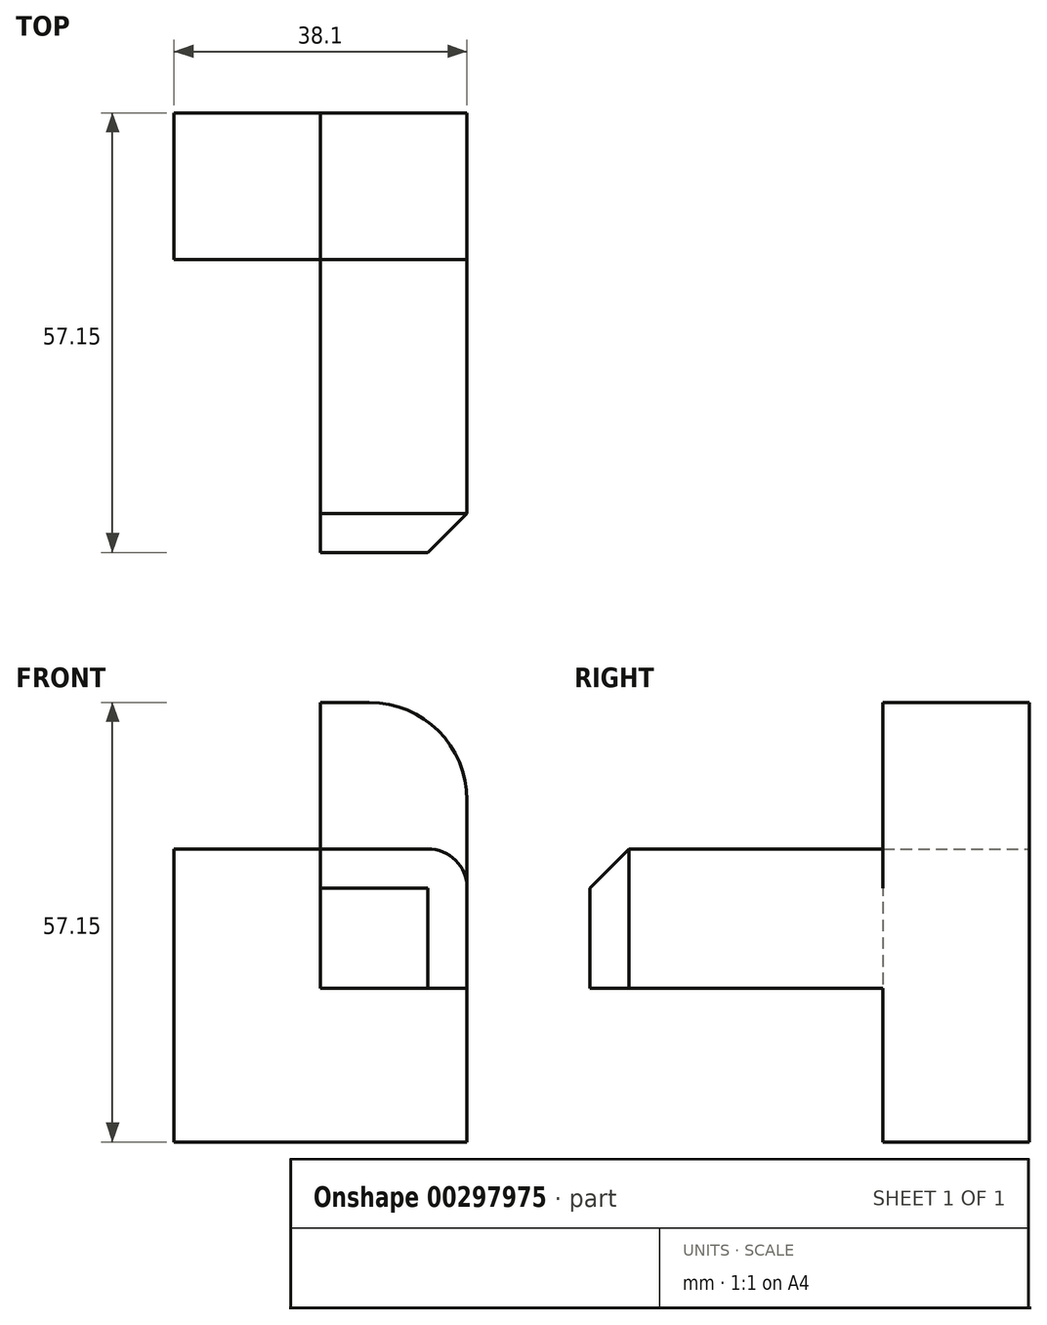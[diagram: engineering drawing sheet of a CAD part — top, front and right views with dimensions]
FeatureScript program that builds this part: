
annotation { "Feature Type Name" : "Feature", "Feature Type Description" : "" }
export const myFeature = defineFeature(function(context is Context, id is Id, definition is map)
    precondition{}
    {
        {
            var Q0;
            Q0=qCreatedBy(makeId("Front.planeOp"),FACE);
            var sketch = newSketch(context, id + "F0", { "sketchPlane" : qUnion([Q0])});
            skLineSegment(sketch, "E0.bottom", {"start": v(0, 0) * mm, "end": v(38.1, 0) * mm});
            skLineSegment(sketch, "E0.top", {"start": v(0, 38.1) * mm, "end": v(19.05, 38.1) * mm});
            skLineSegment(sketch, "E0.left", {"start": v(0, 0) * mm, "end": v(0, 38.1) * mm});
            skLineSegment(sketch, "E0.right", {"start": v(38.1, 0) * mm, "end": v(38.1, 38.1) * mm});
            skLineSegment(sketch, "E1.top", {"start": v(19.05, 57.15) * mm, "end": v(38.1, 57.15) * mm});
            skLineSegment(sketch, "E1.left", {"start": v(19.05, 38.1) * mm, "end": v(19.05, 57.15) * mm});
            skLineSegment(sketch, "E1.right", {"start": v(38.1, 38.1) * mm, "end": v(38.1, 57.15) * mm});
            skSolve(sketch);
        }
        {
            var Q0;
            Q0 = qSketchRegion(id + "F0", true);
            extrude(context, id + "F1", {"entities" : qUnion([Q0]), "depth" : 19.05 * mm});
        }
        {
            var Q0;
            Q0=makeQuery(id+"F1.opExtrude","CAP_FACE",FACE,{"disambiguationData":[OSD([sQuery(id+"F0.wireOp",EDGE,"E0.bottom"),sQuery(id+"F0.wireOp",EDGE,"E0.top"),sQuery(id+"F0.wireOp",EDGE,"E0.left"),sQuery(id+"F0.wireOp",EDGE,"E0.right"),sQuery(id+"F0.wireOp",EDGE,"E1.top"),sQuery(id+"F0.wireOp",EDGE,"E1.left"),sQuery(id+"F0.wireOp",EDGE,"E1.right")])],"isStart":false});
            var sketch = newSketch(context, id + "F2", { "sketchPlane" : qUnion([Q0])});
            skLineSegment(sketch, "E2.bottom", {"start": v(19.05, 38.1) * mm, "end": v(38.1, 38.1) * mm});
            skLineSegment(sketch, "E2.top", {"start": v(19.05, 19.97) * mm, "end": v(38.1, 19.97) * mm});
            skLineSegment(sketch, "E2.left", {"start": v(19.05, 38.1) * mm, "end": v(19.05, 19.97) * mm});
            skLineSegment(sketch, "E2.right", {"start": v(38.1, 38.1) * mm, "end": v(38.1, 19.97) * mm});
            skSolve(sketch);
        }
        {
            var Q0;
            Q0 = qSketchRegion(id + "F2", true);
            extrude(context, id + "F3", {"entities" : qUnion([Q0]), "operationType" : NewBodyOperationType.ADD, "depth" : 38.1 * mm});
        }
        {
            var Q0;
            Q0=makeQuery(id+"F3.opExtrude","SWEPT_EDGE",EDGE,{"disambiguationData":[OSD([sQuery(id+"F0.wireOp",EDGE,"E0.right"),sQuery(id+"F0.wireOp",EDGE,"E1.right"),sQuery(id+"F2.wireOp",EDGE,"E2.bottom"),sQuery(id+"F2.wireOp",EDGE,"E2.right")])]});
            fillet(context, id + "F4", {"entities" : qUnion([Q0]), "radius" : 5.08 * mm, "tangentPropagation" : true, "allowEdgeOverflow" : false});
        }
        {
            var Q0;
            Q0=makeQuery(id+"F3.opExtrude","CAP_EDGE",EDGE,{"disambiguationData":[OSD([sQuery(id+"F2.wireOp",EDGE,"E2.bottom")])],"isStart":false});
            chamfer(context, id + "F5", {"entities" : qUnion([Q0]), "width" : 5.08 * mm, "tangentPropagation" : true});
        }
        {
            var Q0;
            Q0=makeQuery(id+"F1.opExtrude","SWEPT_EDGE",EDGE,{"disambiguationData":[OSD([sQuery(id+"F0.wireOp",EDGE,"E1.top"),sQuery(id+"F0.wireOp",EDGE,"E1.right")])]});
            fillet(context, id + "F6", {"entities" : qUnion([Q0]), "radius" : 12.7 * mm, "tangentPropagation" : true, "allowEdgeOverflow" : false});
        }
    });
